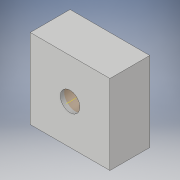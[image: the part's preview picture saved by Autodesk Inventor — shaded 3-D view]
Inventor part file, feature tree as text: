
AUTODESK INVENTOR PART (.ipt)
format: ipt  version: 2019.1 (Build 231200000, 200)  size: 103,424 bytes
history: native  units: in
note: dims shown in document units (in); Inventor stores cm internally (conversion verified against a paired STEP export)
features: sketch x2, extrude x1, plane x1, revolve x1
ambient origin geometry x8: Origin, YZ Plane, XZ Plane, XY Plane, X Axis, Y Axis, Z Axis, Center Point
bodies: Solid1 (feature_tree)
feature tree (5):
  extrude  "Extrusion1"  Depth=1.0in TaperAngle=0.0deg
  plane  "Work Plane1"
  revolve  "Revolution1"  Angle=90.0deg
  sketch  "Sketch1"  dims[d0=2.0in d1=1.0in d2=0.0in]
  sketch  "Sketch2"  dims[d3=-0.125in d4=90.0deg d5=0.275in]
